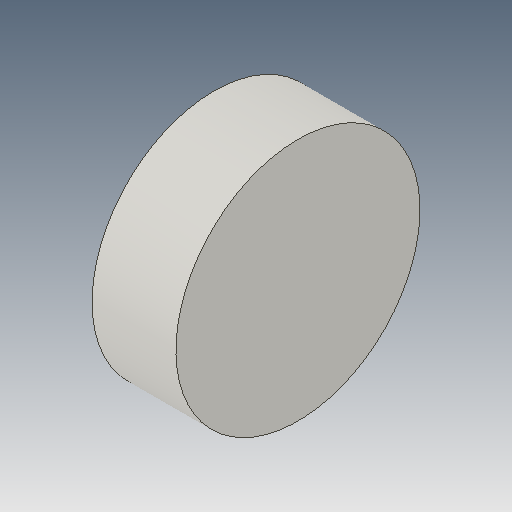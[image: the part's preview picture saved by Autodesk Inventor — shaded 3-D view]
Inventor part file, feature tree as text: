
AUTODESK INVENTOR PART (.ipt)
format: ipt  version: 2018 (Build 220112000, 112)  size: 82,944 bytes
history: native  units: in
note: dims shown in document units (in); Inventor stores cm internally (conversion verified against a paired STEP export)
features: other x3, sketch x1
ambient origin geometry x8: Origin, YZ Plane, XZ Plane, XY Plane, X Axis, Y Axis, Z Axis, Center Point
bodies: Solid1 (feature_tree)
feature tree (4):
  other  "Wheel.ipt"
  other  "Solid1::Wheel.ipt"
  other  "TaggingFeature1"
  sketch  "Sketch1"  dims[d0=0.3937in]
